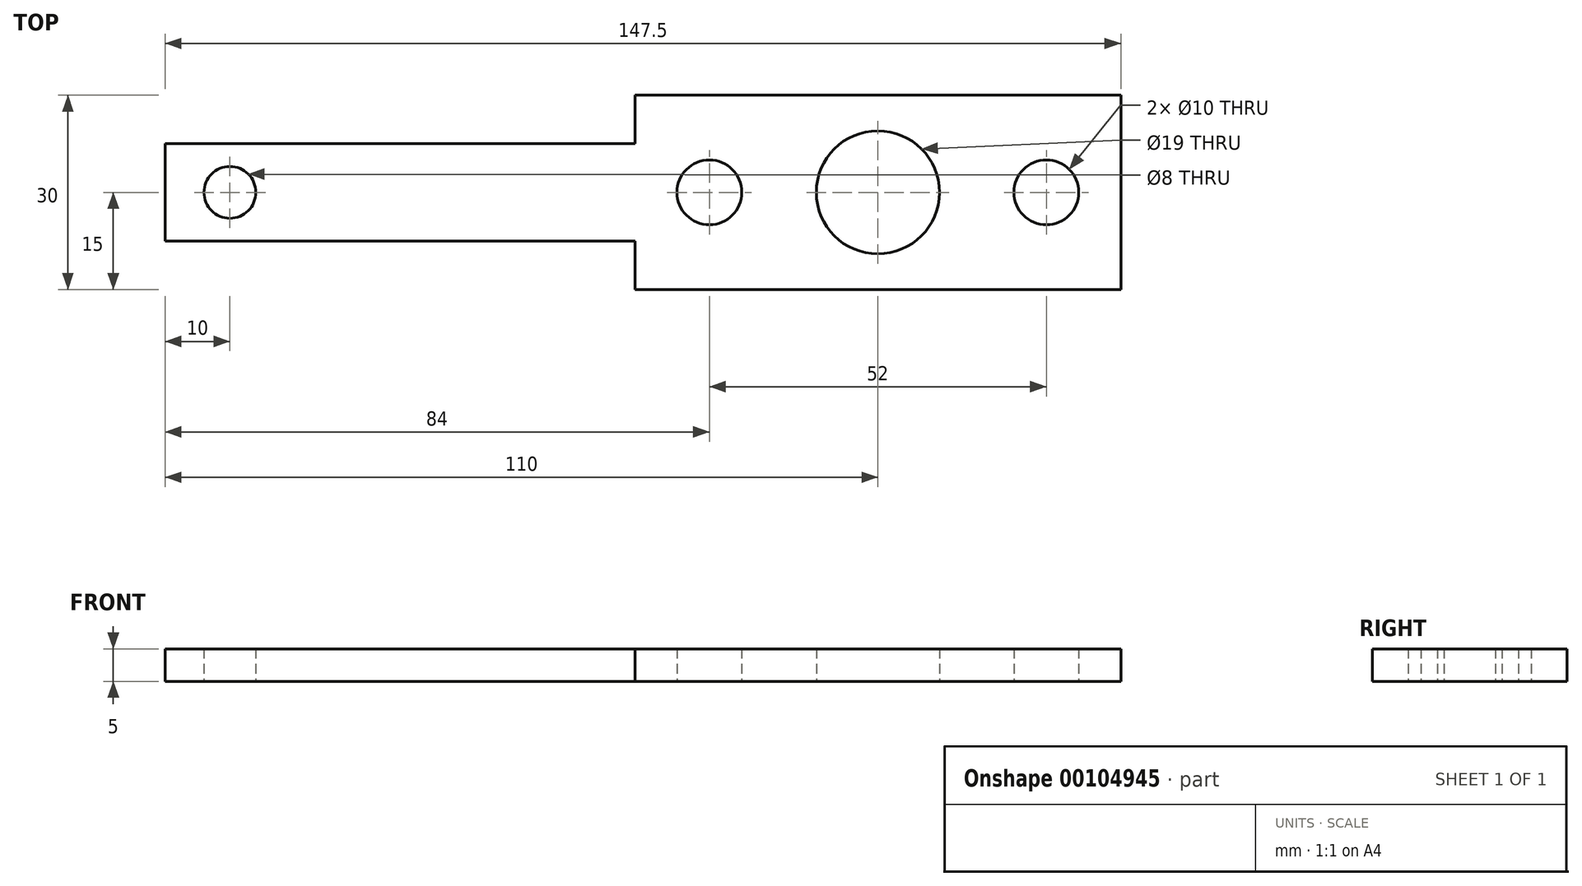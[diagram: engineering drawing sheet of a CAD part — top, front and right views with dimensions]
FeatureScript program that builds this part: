
annotation { "Feature Type Name" : "Feature", "Feature Type Description" : "" }
export const myFeature = defineFeature(function(context is Context, id is Id, definition is map)
    precondition{}
    {
        {
            var Q0;
            Q0=qCreatedBy(makeId("Top.planeOp"),FACE);
            var sketch = newSketch(context, id + "F0", { "sketchPlane" : qUnion([Q0])});
            skCircle(sketch, "E0", {"center": v(-26, 0) * mm, "radius": 5 * mm});
            skCircle(sketch, "E1", {"center": v(26, 0) * mm, "radius": 5 * mm});
            skLineSegment(sketch, "E2", {"start": v(-37.5, 15) * mm, "end": v(37.5, 15) * mm});
            skLineSegment(sketch, "E3", {"start": v(37.5, 15) * mm, "end": v(37.5, 0) * mm});
            skLineSegment(sketch, "E4", {"start": v(37.5, 0) * mm, "end": v(37.5, -15) * mm});
            skLineSegment(sketch, "E5", {"start": v(37.5, -15) * mm, "end": v(-37.5, -15) * mm});
            skCircle(sketch, "E6", {"center": v(0, 0) * mm, "radius": 9.5 * mm});
            skPoint(sketch, "E7.start.orphan", {"position": v(-37.5, 0) * mm});
            skLineSegment(sketch, "E8", {"start": v(-37.5, 15) * mm, "end": v(-37.5, 7.5) * mm});
            skLineSegment(sketch, "E9", {"start": v(-37.5, 7.5) * mm, "end": v(-110, 7.5) * mm});
            skLineSegment(sketch, "E10", {"start": v(-110, 7.5) * mm, "end": v(-110, -7.5) * mm});
            skLineSegment(sketch, "E11", {"start": v(-110, -7.5) * mm, "end": v(-37.5, -7.5) * mm});
            skLineSegment(sketch, "E12", {"start": v(-37.5, -7.5) * mm, "end": v(-37.5, -15) * mm});
            skCircle(sketch, "E13", {"center": v(-100, 0) * mm, "radius": 4 * mm});
            skSolve(sketch);
        }
        {
            var Q0;
            Q0 = qSketchRegion(id + "F0", true);
            extrude(context, id + "F1", {"entities" : qUnion([Q0]), "depth" : 5 * mm});
        }
    });
